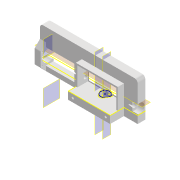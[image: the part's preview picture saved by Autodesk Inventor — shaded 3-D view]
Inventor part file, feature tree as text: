
AUTODESK INVENTOR PART (.ipt)
format: ipt  version: 2022 (Build 260153000, 153)  size: 518,144 bytes
history: native  units: mm
features: sketch x23, extrude x22, reference x11, projected_geometry x10, other x10, plane x8, fillet x2, chamfer x1, mirror x1, hole x1
ambient origin geometry x8: Origin, YZ Plane, XZ Plane, XY Plane, X Axis, Y Axis, Z Axis, Center Point
bodies: Solid1 (feature_tree)
feature tree (89):
  extrude  "Extrusion1"  Depth=10.0mm
  fillet  "Fillet1"  Radius=10.0mm
  extrude  "Extrusion2"  Depth=4.0mm
  extrude  "Extrusion3"  Depth=20.0mm
  plane  "Work Plane1"
  plane  "Work Plane2"
  chamfer  "Chamfer1"  [1 undecoded]
  extrude  "Extrusion4"  Depth=10.0mm
  extrude  "Extrusion5"  Depth=8.0mm
  extrude  "Extrusion6"  Depth=5.0mm TaperAngle=0.0deg
  plane  "Work Plane3"
  extrude  "Extrusion12"  Depth=18.0mm TaperAngle=0.0deg
  extrude  "Extrusion13"  Depth=2.0mm
  mirror  "Mirror1"
  plane  "Work Plane4"
  plane  "Work Plane5"
  extrude  "Extrusion21"  Depth=2.0mm
  extrude  "Extrusion22"  Depth=12.0mm
  plane  "Arbeitsebene7"
  extrude  "Extrusion27"  Depth=7.0mm
  extrude  "Extrusion28"  Depth=10.0mm
  extrude  "Extrusion29"  Depth=6.0mm
  fillet  "Rundung6"  Radius=6.0mm
  sketch  "Skizze32"  dims[d61=30.0mm d62=-0.523599mm d63=12.0mm]
  plane  "Arbeitsebene8"
  extrude  "Extrusion30"  TaperAngle=0.0deg  [1 undecoded]
  extrude  "Extrusion31"  Depth=40.0mm TaperAngle=0.0deg
  extrude  "Extrusion32"  Depth=0.5mm
  extrude  "Extrusion33"  Depth=2.0mm
  sketch  "Skizze36"  dims[d108=6.0mm d109=0.0mm d110=0.0mm]
  plane  "Arbeitsebene9"
  extrude  "Extrusion34"  TaperAngle=45.0deg  [1 undecoded]
  extrude  "Extrusion35"  Depth=9.0mm
  hole  "Bohrung2"  [1 undecoded]
  extrude  "Extrusion36"  Depth=9.0mm TaperAngle=0.0deg
  extrude  "Extrusion37"  Depth=17.0mm
  extrude  "Extrusion38"  Depth=9.0mm TaperAngle=0.0deg
  sketch  "Sketch1"  dims[d0=127.8mm d1=85.5mm d2=10.0mm d3=0.0mm]
  sketch  "Sketch2"  dims[d4=4.0mm d5=51.0mm]
  projected_geometry  "Projected Loop1"
  sketch  "Sketch3"  dims[d6=25.0mm d7=20.0mm]
  projected_geometry  "Projected Loop2"
  sketch  "Sketch4"  dims[d8=15.0mm]
  projected_geometry  "Projected Loop3"
  sketch  "Sketch5"  dims[d9=6.0mm]
  sketch  "Sketch6"  dims[d10=0.0mm]
  reference  "Reference2"
  sketch  "Sketch12"  dims[d11=1.5mm d12=0.0mm d13=0.0mm]
  reference  "Reference4"
  sketch  "Sketch13"  dims[d14=4.0mm d15=2.0mm d16=45.0deg d17=10.0mm]
  sketch  "Sketch22"  dims[d18=8.0mm d19=0.0mm d20=1.9mm]
  projected_geometry  "Projected Loop8"
  sketch  "Sketch23"  dims[d21=4.0mm d22=5.0mm d23=0.0mm]
  projected_geometry  "Projected Loop9"
  reference  "Reference11"
  sketch  "Skizze28"  dims[d27=20.0mm d28=18.0mm d29=0.0mm]
  sketch  "Skizze29"  dims[d38=10.0mm d52=2.0mm]
  reference  "Referenz13"
  sketch  "Skizze30"  dims[d53=2.0mm d54=2.0mm]
  reference  "Referenz14"
  reference  "Referenz16"
  sketch  "Skizze33"  dims[d64=7.0mm d65=0.0mm d100=7.0mm]
  reference  "Referenz17"
  sketch  "Skizze34"  dims[d101=10.0mm d102=0.0mm d103=11.8mm]
  reference  "Referenz18"
  sketch  "Skizze35"  dims[d105=2.8mm d106=2.8mm d107=6.0mm]
  projected_geometry  "Projizierte Kontur15"
  reference  "Referenz19"
  reference  "Referenz20"
  sketch  "Skizze37"  dims[d142=0.5mm d143=40.0mm d144=0.0mm]
  reference  "Referenz21"
  sketch  "Skizze38"  dims[d145=8.0mm d146=0.0mm d147=0.5mm]
  projected_geometry  "Projizierte Kontur16"
  sketch  "Skizze39"  dims[d148=1.0mm d149=0.0mm d150=2.0mm]
  projected_geometry  "Projizierte Kontur17"
  sketch  "Skizze40"  dims[d151=45.0deg d152=45.0deg]
  projected_geometry  "Projizierte Kontur18"
  sketch  "Skizze41"  dims[d153=8.0mm d154=0.0mm d155=7.0mm d156=3.0mm d157=0.0mm d158=30.0mm d159=0.0mm d160=17.0mm d161=15.0mm d162=0.0mm d163=0.5mm d164=15.0mm d165=0.0mm d166=8.0mm d167=10.0mm d168=0.0mm d169=2.8mm d170=6.0mm d171=4.0mm d172=2.0mm d173=90.0deg d174=8.0mm d175=20.594885mm d176=0.0mm d177=0.0mm d178=1.0mm d179=0.0mm d180=2.8mm d181=2.8mm d182=2.8mm d183=2.8mm d184=72.615mm d185=5.0mm d186=5.0mm d187=3.0mm d188=3.0mm d189=2.8mm d190=2.8mm d191=3.0mm d192=2.8mm d193=2.8mm d194=5.0mm d195=9.0mm d197=0.0mm d198=0.0mm]
  projected_geometry  "Projizierte Kontur19"
  other  "<userpath>\Documents\GitHub\Guinardia\INVENTOR\Assembly_Guinardia_V1.iam"
  other  "Assembly_Guinardia_V1.iam"
  other  "00_CCTV_lens_M12_25mm_5mp:1"
  other  "00_PipetteTip200ul-1:2"
  other  "00_NEMA8:1"
  other  "00_SM05FC2-Step:1"
  other  "00_CCTV_lens_M12_25mm_5mp:2"
  other  "00_HuaweiP30_Telelens_prismonly:1"
  other  "<userpath>\Documents\Inventor\Guinardia\INVENTOR\Assembly_Guinardia_V0.iam"
  other  "Assembly_Guinardia_V0.iam"
note: 4 required parameter values undecoded (feature->parameter linkage not recoverable at this tier; creation-order binding heuristic only, values carry confidence <= 0.55)
